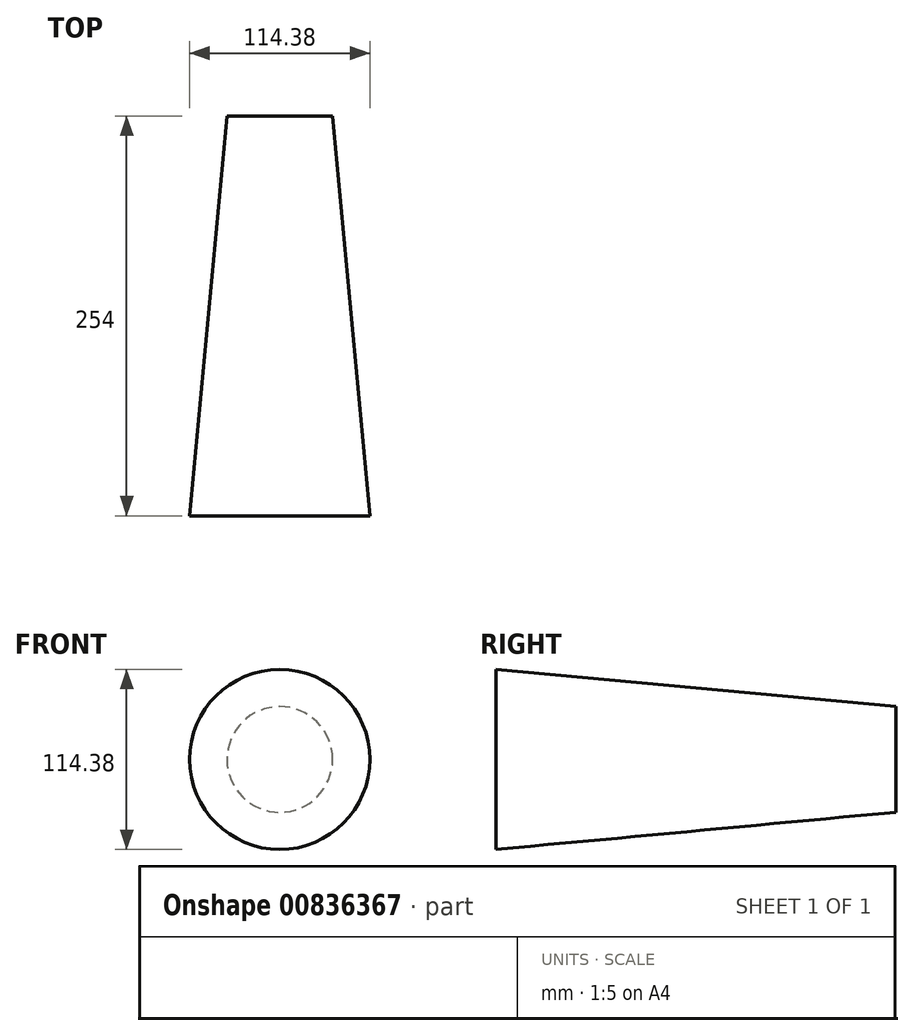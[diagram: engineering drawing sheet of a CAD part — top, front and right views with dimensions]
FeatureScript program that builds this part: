
annotation { "Feature Type Name" : "Feature", "Feature Type Description" : "" }
export const myFeature = defineFeature(function(context is Context, id is Id, definition is map)
    precondition{}
    {
        {
            var Q0;
            Q0=qCreatedBy(makeId("Front.planeOp"),FACE);
            var sketch = newSketch(context, id + "F0", { "sketchPlane" : qUnion([Q0])});
            skCircle(sketch, "E0", {"center": v(0, 0) * mm, "radius": 33.54 * mm});
            skSolve(sketch);
        }
        {
            var Q0;
            Q0=qCreatedBy(makeId("Front.planeOp"),FACE);
            cPlane(context, id + "F1", {"entities" : qUnion([Q0]), "cplaneType" : CPlaneType.OFFSET, "offset" : 254 * mm, "width" : 152.4 * mm, "height" : 152.4 * mm});
        }
        {
            var Q0;
            Q0=qCreatedBy(id+"F1.planeOp",FACE);
            var sketch = newSketch(context, id + "F2", { "sketchPlane" : qUnion([Q0])});
            skCircle(sketch, "E1.0", {"center": v(0, 0) * mm, "radius": 33.54 * mm, "construction": true});
            skCircle(sketch, "E2", {"center": v(0, 0) * mm, "radius": 57.19 * mm});
            skSolve(sketch);
        }
        {
            var Q0;
            Q0=makeQuery(id+"F0.imprint","IMPRINT",FACE,{"disambiguationData":[TD([[makeQuery(id+"F0.imprint","IMPRINT",EDGE,{"derivedFrom":sQuery(id+"F0.wireOp",EDGE,"E0")}),1.0]])]});
            var Q1;
            Q1=makeQuery(id+"F2.imprint","IMPRINT",FACE,{"disambiguationData":[TD([[makeQuery(id+"F2.imprint","IMPRINT",EDGE,{"derivedFrom":sQuery(id+"F2.wireOp",EDGE,"E2")}),1.0]])]});
            loft(context, id + "F3", {"sheetProfilesArray" : [{ "sheetProfileEntities" : qUnion([Q0]) }, { "sheetProfileEntities" : qUnion([Q1]) }]});
        }
    });
